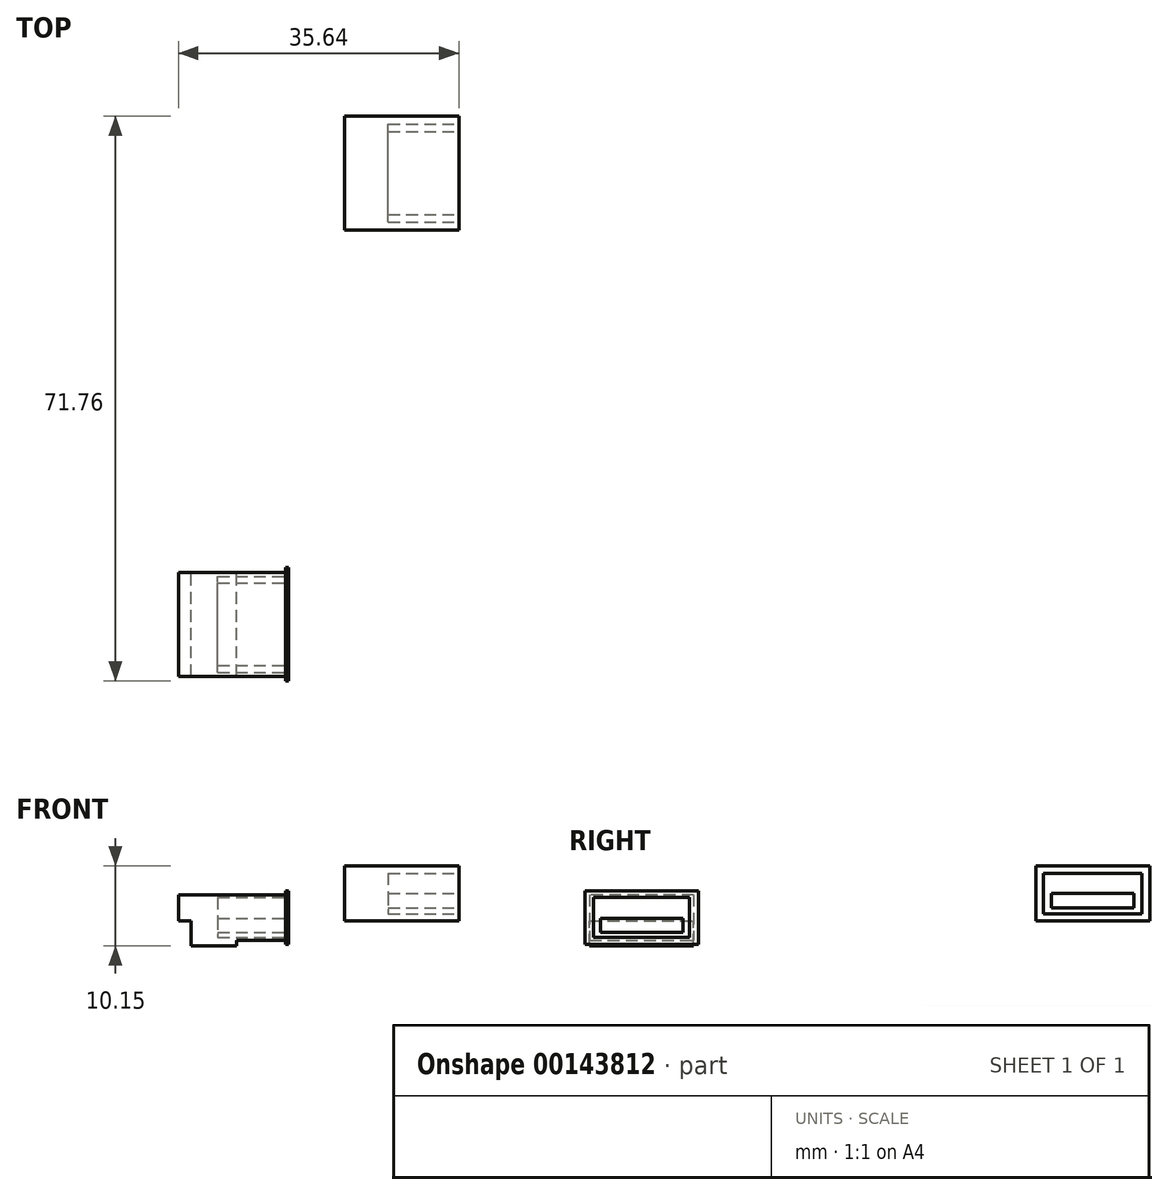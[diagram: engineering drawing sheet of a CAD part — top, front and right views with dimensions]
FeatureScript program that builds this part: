
annotation { "Feature Type Name" : "Feature", "Feature Type Description" : "" }
export const myFeature = defineFeature(function(context is Context, id is Id, definition is map)
    precondition{}
    {
        {
            var Q0;
            Q0=qCreatedBy(makeId("Top.planeOp"),FACE);
            var sketch = newSketch(context, id + "F0", { "sketchPlane" : qUnion([Q0])});
            skLineSegment(sketch, "E0", {"start": v(0, 0) * mm, "end": v(88.3, 0) * mm, "construction": true});
            skLineSegment(sketch, "E1", {"start": v(0, 0) * mm, "end": v(0, 13.55) * mm});
            skLineSegment(sketch, "E2", {"start": v(3, 16.55) * mm, "end": v(84.8, 16.55) * mm});
            skLineSegment(sketch, "E3", {"start": v(88.3, 1.25) * mm, "end": v(88.3, 0) * mm});
            skLineSegment(sketch, "E4", {"start": v(3, 16.55) * mm, "end": v(0, 13.55) * mm});
            skLineSegment(sketch, "E5.0.MirrorCS", {"start": v(0, 0) * mm, "end": v(0, -13.55) * mm});
            skLineSegment(sketch, "E6.0.MirrorCS", {"start": v(3, -16.55) * mm, "end": v(0, -13.55) * mm});
            skLineSegment(sketch, "E7.0.MirrorCS", {"start": v(3, -16.55) * mm, "end": v(85.3, -16.55) * mm});
            skArc(sketch, "E8.0.MirrorCS", {"start": v(88.3, -13.55) * mm, "mid": v(87.42, -15.67) * mm, "end": v(85.3, -16.55) * mm});
            skLineSegment(sketch, "E9.0.MirrorCS", {"start": v(88.3, -13.55) * mm, "end": v(88.3, 0) * mm});
            skLineSegment(sketch, "E10", {"start": v(84.8, 16.55) * mm, "end": v(84.8, 14.45) * mm});
            skLineSegment(sketch, "E11", {"start": v(84.8, 14.45) * mm, "end": v(76.2, 14.45) * mm});
            skLineSegment(sketch, "E12", {"start": v(76.2, 14.45) * mm, "end": v(76.2, 1.25) * mm});
            skLineSegment(sketch, "E13", {"start": v(76.2, 1.25) * mm, "end": v(88.3, 1.25) * mm});
            skLineSegment(sketch, "E14.bottom", {"start": v(52.1, 8.78) * mm, "end": v(64.1, 8.78) * mm});
            skLineSegment(sketch, "E14.top", {"start": v(52.1, -10.22) * mm, "end": v(64.1, -10.22) * mm});
            skLineSegment(sketch, "E14.left", {"start": v(52.1, 8.78) * mm, "end": v(52.1, -10.22) * mm});
            skLineSegment(sketch, "E14.right", {"start": v(64.1, 8.78) * mm, "end": v(64.1, -10.22) * mm});
            skLineSegment(sketch, "E15.bottom", {"start": v(69.8, -2.75) * mm, "end": v(81.8, -2.75) * mm});
            skLineSegment(sketch, "E15.top", {"start": v(69.8, -14.75) * mm, "end": v(81.8, -14.75) * mm});
            skLineSegment(sketch, "E15.left", {"start": v(69.8, -2.75) * mm, "end": v(69.8, -14.75) * mm});
            skLineSegment(sketch, "E15.right", {"start": v(81.8, -2.75) * mm, "end": v(81.8, -14.75) * mm});
            skLineSegment(sketch, "E16.bottom", {"start": v(12.1, 12.55) * mm, "end": v(25.6, 12.55) * mm});
            skLineSegment(sketch, "E16.top", {"start": v(12.1, 5.05) * mm, "end": v(25.6, 5.05) * mm});
            skLineSegment(sketch, "E16.left", {"start": v(12.1, 12.55) * mm, "end": v(12.1, 5.05) * mm});
            skLineSegment(sketch, "E16.right", {"start": v(25.6, 12.55) * mm, "end": v(25.6, 5.05) * mm});
            skLineSegment(sketch, "E17.bottom", {"start": v(12.1, -6.55) * mm, "end": v(25.6, -6.55) * mm});
            skLineSegment(sketch, "E17.top", {"start": v(12.1, -14.05) * mm, "end": v(25.6, -14.05) * mm});
            skLineSegment(sketch, "E17.left", {"start": v(12.1, -6.55) * mm, "end": v(12.1, -14.05) * mm});
            skLineSegment(sketch, "E17.right", {"start": v(25.6, -6.55) * mm, "end": v(25.6, -14.05) * mm});
            skLineSegment(sketch, "E18", {"start": v(44.1, 9.25) * mm, "end": v(54, -0.65) * mm});
            skLineSegment(sketch, "E19", {"start": v(54, -0.65) * mm, "end": v(44.1, -10.55) * mm});
            skLineSegment(sketch, "E20", {"start": v(44.1, -10.55) * mm, "end": v(34.2, -0.65) * mm});
            skLineSegment(sketch, "E21", {"start": v(34.2, -0.65) * mm, "end": v(44.1, 9.25) * mm});
            skLineSegment(sketch, "E22.bottom", {"start": v(28, -16.25) * mm, "end": v(29.4, -16.25) * mm});
            skLineSegment(sketch, "E22.top", {"start": v(28, -13.75) * mm, "end": v(32.7, -13.75) * mm});
            skLineSegment(sketch, "E22.left", {"start": v(28, -16.25) * mm, "end": v(28, -13.75) * mm});
            skLineSegment(sketch, "E22.right", {"start": v(32.7, -16.25) * mm, "end": v(32.7, -13.75) * mm});
            skLineSegment(sketch, "E23", {"start": v(31.3, -16.25) * mm, "end": v(31.3, -17.55) * mm});
            skLineSegment(sketch, "E24", {"start": v(31.3, -17.55) * mm, "end": v(29.4, -17.55) * mm});
            skLineSegment(sketch, "E25", {"start": v(29.4, -17.55) * mm, "end": v(29.4, -16.25) * mm});
            skLineSegment(sketch, "E26.trimOffspring", {"start": v(31.3, -16.25) * mm, "end": v(32.7, -16.25) * mm});
            skLineSegment(sketch, "E27", {"start": v(29.4, -16.25) * mm, "end": v(31.3, -16.25) * mm});
            skLineSegment(sketch, "E28", {"start": v(70.8, -1.75) * mm, "end": v(55.9, -1.75) * mm});
            skLineSegment(sketch, "E29", {"start": v(55.9, -1.75) * mm, "end": v(55.9, -16.55) * mm});
            skLineSegment(sketch, "E30", {"start": v(55.9, -16.55) * mm, "end": v(58.9, -16.55) * mm});
            skLineSegment(sketch, "E31", {"start": v(58.9, -16.55) * mm, "end": v(61.8, -15.75) * mm});
            skLineSegment(sketch, "E32", {"start": v(61.8, -15.75) * mm, "end": v(70.8, -15.75) * mm});
            skLineSegment(sketch, "E33", {"start": v(70.8, -15.75) * mm, "end": v(70.8, -1.75) * mm});
            skSolve(sketch);
        }
        {
            var Q0;
            Q0=qCreatedBy(makeId("Top.planeOp"),FACE);
            var sketch = newSketch(context, id + "F1", { "sketchPlane" : qUnion([Q0])});
            skLineSegment(sketch, "E34", {"start": v(88.3, 1.25) * mm, "end": v(76.3, 1.25) * mm});
            skLineSegment(sketch, "E35", {"start": v(76.3, 1.25) * mm, "end": v(76.3, 14.45) * mm});
            skLineSegment(sketch, "E36", {"start": v(76.3, 14.45) * mm, "end": v(88.3, 14.45) * mm});
            skLineSegment(sketch, "E37", {"start": v(88.3, 14.45) * mm, "end": v(88.3, 1.25) * mm});
            skLineSegment(sketch, "E38", {"start": v(88.3, 14.45) * mm, "end": v(88.3, 15.05) * mm});
            skLineSegment(sketch, "E39", {"start": v(88.3, 15.05) * mm, "end": v(88.7, 15.05) * mm});
            skLineSegment(sketch, "E40", {"start": v(88.7, 15.05) * mm, "end": v(88.7, 0.65) * mm});
            skLineSegment(sketch, "E41", {"start": v(88.7, 0.65) * mm, "end": v(88.3, 0.65) * mm});
            skLineSegment(sketch, "E42", {"start": v(88.3, 0.65) * mm, "end": v(88.3, 1.25) * mm});
            skLineSegment(sketch, "E43", {"start": v(76.3, 14.45) * mm, "end": v(74.7, 14.45) * mm});
            skLineSegment(sketch, "E44", {"start": v(74.7, 14.45) * mm, "end": v(74.7, 1.25) * mm});
            skLineSegment(sketch, "E45", {"start": v(74.7, 1.25) * mm, "end": v(76.3, 1.25) * mm});
            skLineSegment(sketch, "E46", {"start": v(82.1, 1.25) * mm, "end": v(82.1, 14.45) * mm});
            skSolve(sketch);
        }
        {
            var Q0;
            Q0=makeQuery(id+"F1.imprint","IMPRINT",FACE,{"disambiguationData":[TD([[makeQuery(id+"F1.imprint","IMPRINT",EDGE,{"derivedFrom":sQuery(id+"F1.wireOp",EDGE,"E34")}),-1.0]])]});
            var Q1;
            Q1=makeQuery(id+"F1.imprint","IMPRINT",FACE,{"disambiguationData":[TD([[makeQuery(id+"F1.imprint","IMPRINT",EDGE,{"derivedFrom":sQuery(id+"F1.wireOp",EDGE,"E35")}),1.0]])]});
            extrude(context, id + "F2", {"entities" : qUnion([Q0, Q1]), "depth" : (4.8 - 1.45) * mm});
        }
        {
            var Q0;
            {var subQ2=sQuery(id+"F1.wireOp",EDGE,"E35");Q0=makeQuery(id+"F1.imprint","IMPRINT",FACE,{"disambiguationData":[TD([[makeQuery(id+"F1.imprint","IMPRINT",EDGE,{"derivedFrom":subQ2}),-1.0]])]});}
            extrude(context, id + "F3", {"entities" : qUnion([Q0]), "operationType" : NewBodyOperationType.ADD, "oppositeDirection" : true, "depth" : (6.5 - 4.8 + 1.45) * mm});
        }
        {
            var Q0;
            {var subQ1=sQuery(id+"F1.wireOp",EDGE,"E37");Q0=makeQuery(id+"F1.imprint","IMPRINT",FACE,{"disambiguationData":[TD([[makeQuery(id+"F1.imprint","IMPRINT",EDGE,{"derivedFrom":subQ1}),-1.0]])]});}
            extrude(context, id + "F4", {"entities" : qUnion([Q0]), "operationType" : NewBodyOperationType.ADD, "oppositeDirection" : true, "depth" : 2.45 * mm});
        }
        {
            var Q0;
            Q0=makeQuery(id+"F1.imprint","IMPRINT",FACE,{"disambiguationData":[TD([[makeQuery(id+"F1.imprint","IMPRINT",EDGE,{"derivedFrom":sQuery(id+"F1.wireOp",EDGE,"E37")}),1.0]])]});
            extrude(context, id + "F5", {"entities" : qUnion([Q0]), "operationType" : NewBodyOperationType.ADD, "depth" : 3.85 * mm, "hasSecondDirection" : true, "secondDirectionOppositeDirection" : true, "secondDirectionDepth" : 2.95 * mm});
        }
        {
            var Q0;
            Q0=makeQuery(id+"F5.opExtrude","SWEPT_FACE",FACE,{"disambiguationData":[OSD([sQuery(id+"F1.wireOp",EDGE,"E40")])]});
            var sketch = newSketch(context, id + "F6", { "sketchPlane" : qUnion([Q0])});
            skLineSegment(sketch, "E47.bottom", {"start": v(1.75, 3) * mm, "end": v(13.95, 3) * mm});
            skLineSegment(sketch, "E47.top", {"start": v(1.75, -2.1) * mm, "end": v(13.95, -2.1) * mm});
            skLineSegment(sketch, "E47.left", {"start": v(1.75, 3) * mm, "end": v(1.75, -2.1) * mm});
            skLineSegment(sketch, "E47.right", {"start": v(13.95, 3) * mm, "end": v(13.95, -2.1) * mm});
            skLineSegment(sketch, "E48.bottom", {"start": v(2.6, 0.35) * mm, "end": v(13.1, 0.35) * mm});
            skLineSegment(sketch, "E48.top", {"start": v(2.6, -1.45) * mm, "end": v(13.1, -1.45) * mm});
            skLineSegment(sketch, "E48.left", {"start": v(2.6, 0.35) * mm, "end": v(2.6, -1.45) * mm});
            skLineSegment(sketch, "E48.right", {"start": v(13.1, 0.35) * mm, "end": v(13.1, -1.45) * mm});
            skSolve(sketch);
        }
        {
            var Q0;
            Q0=makeQuery(id+"F6.imprint","IMPRINT",FACE,{"disambiguationData":[TD([[makeQuery(id+"F6.imprint","IMPRINT",EDGE,{"derivedFrom":sQuery(id+"F6.wireOp",EDGE,"E47.bottom")}),-1.0]])]});
            extrude(context, id + "F7", {"entities" : qUnion([Q0]), "operationType" : NewBodyOperationType.REMOVE, "oppositeDirection" : true, "depth" : 9 * mm});
        }
        {
            var Q0;
            Q0=qCreatedBy(makeId("Top.planeOp"),FACE);
            var sketch = newSketch(context, id + "F8", { "sketchPlane" : qUnion([Q0])});
            skLineSegment(sketch, "E49.bottom", {"start": v(95.79, 57.91) * mm, "end": v(110.34, 57.91) * mm});
            skLineSegment(sketch, "E49.top", {"start": v(95.79, 72.41) * mm, "end": v(110.34, 72.41) * mm});
            skLineSegment(sketch, "E49.left", {"start": v(95.79, 57.91) * mm, "end": v(95.79, 72.41) * mm});
            skLineSegment(sketch, "E49.right", {"start": v(110.34, 57.91) * mm, "end": v(110.34, 72.41) * mm});
            skSolve(sketch);
        }
        {
            var Q0;
            Q0=makeQuery(id+"F8.imprint","IMPRINT",FACE,{"disambiguationData":[TD([[makeQuery(id+"F8.imprint","IMPRINT",EDGE,{"derivedFrom":sQuery(id+"F8.wireOp",EDGE,"E49.bottom")}),1.0]])]});
            extrude(context, id + "F9", {"entities" : qUnion([Q0]), "depth" : 7 * mm});
        }
        {
            var Q0;
            Q0=makeQuery(id+"F9.opExtrude","SWEPT_FACE",FACE,{"disambiguationData":[OSD([sQuery(id+"F8.wireOp",EDGE,"E49.right")])]});
            var sketch = newSketch(context, id + "F10", { "sketchPlane" : qUnion([Q0])});
            skLineSegment(sketch, "E50.bottom", {"start": v(58.91, 6.06) * mm, "end": v(71.41, 6.06) * mm});
            skLineSegment(sketch, "E50.top", {"start": v(58.91, 0.94) * mm, "end": v(71.41, 0.94) * mm});
            skLineSegment(sketch, "E50.left", {"start": v(58.91, 6.06) * mm, "end": v(58.91, 0.94) * mm});
            skLineSegment(sketch, "E50.right", {"start": v(71.41, 6.06) * mm, "end": v(71.41, 0.94) * mm});
            skLineSegment(sketch, "E51.bottom", {"start": v(59.91, 3.5) * mm, "end": v(70.41, 3.5) * mm});
            skLineSegment(sketch, "E51.top", {"start": v(59.91, 1.7) * mm, "end": v(70.41, 1.7) * mm});
            skLineSegment(sketch, "E51.left", {"start": v(59.91, 3.5) * mm, "end": v(59.91, 1.7) * mm});
            skLineSegment(sketch, "E51.right", {"start": v(70.41, 3.5) * mm, "end": v(70.41, 1.7) * mm});
            skSolve(sketch);
        }
        {
            var Q0;
            Q0=makeQuery(id+"F10.imprint","IMPRINT",FACE,{"disambiguationData":[TD([[makeQuery(id+"F10.imprint","IMPRINT",EDGE,{"derivedFrom":sQuery(id+"F10.wireOp",EDGE,"E50.bottom")}),-1.0]])]});
            extrude(context, id + "F11", {"entities" : qUnion([Q0]), "operationType" : NewBodyOperationType.REMOVE, "oppositeDirection" : true, "depth" : 9 * mm});
        }
    });
